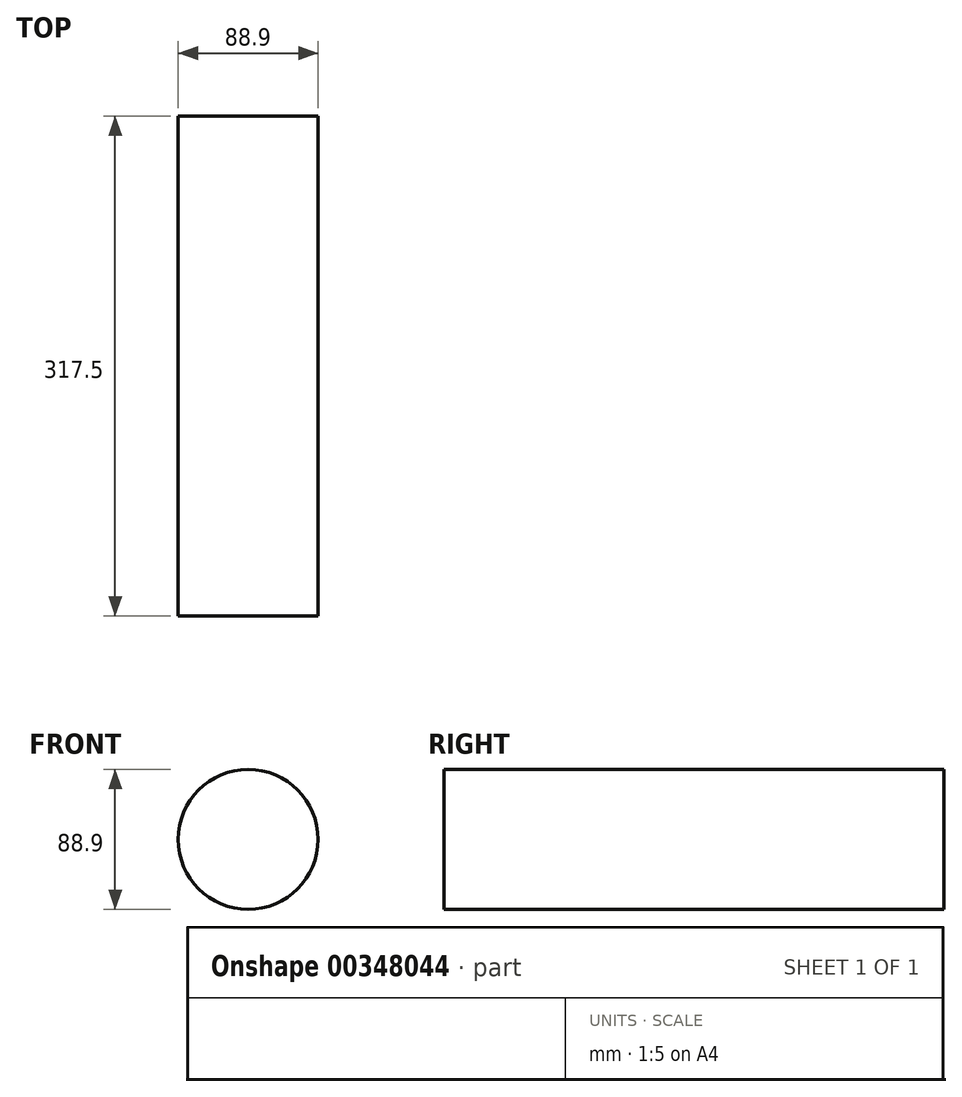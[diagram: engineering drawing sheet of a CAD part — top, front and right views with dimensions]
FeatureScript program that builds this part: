
annotation { "Feature Type Name" : "Feature", "Feature Type Description" : "" }
export const myFeature = defineFeature(function(context is Context, id is Id, definition is map)
    precondition{}
    {
        {
            var Q0;
            Q0=qCreatedBy(makeId("Front.planeOp"),FACE);
            var sketch = newSketch(context, id + "F0", { "sketchPlane" : qUnion([Q0])});
            skCircle(sketch, "E0", {"center": v(0, 0) * mm, "radius": 44.45 * mm});
            skSolve(sketch);
        }
        {
            var Q0;
            Q0 = qSketchRegion(id + "F0", true);
            extrude(context, id + "F1", {"entities" : qUnion([Q0]), "depth" : 317.5 * mm});
        }
    });
